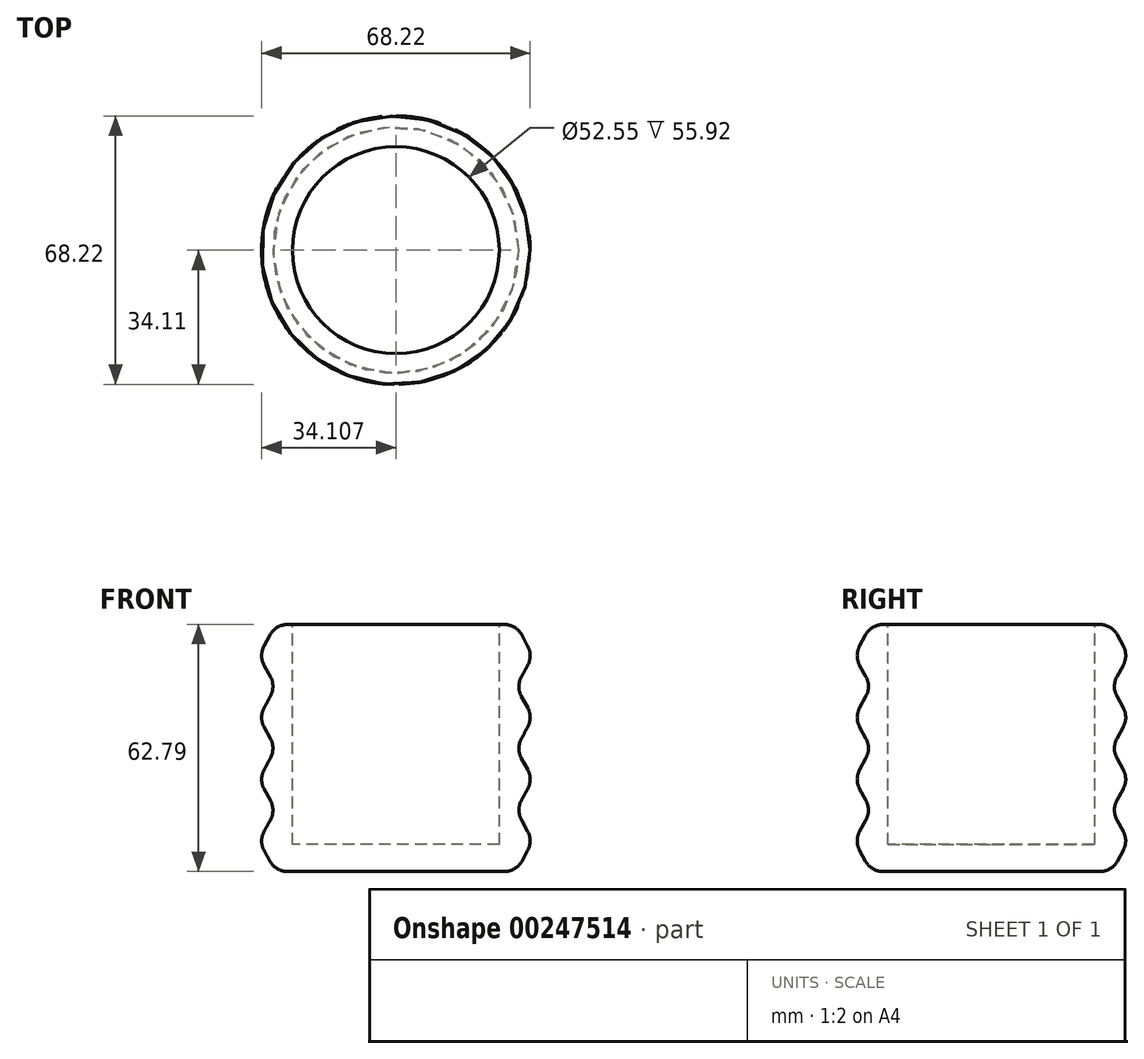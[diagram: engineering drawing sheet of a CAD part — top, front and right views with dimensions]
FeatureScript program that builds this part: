
annotation { "Feature Type Name" : "Feature", "Feature Type Description" : "" }
export const myFeature = defineFeature(function(context is Context, id is Id, definition is map)
    precondition{}
    {
        {
            var Q0;
            Q0=qCreatedBy(makeId("Front.planeOp"),FACE);
            var sketch = newSketch(context, id + "F0", { "sketchPlane" : qUnion([Q0])});
            skLineSegment(sketch, "E0", {"start": v(-1.87, 0) * mm, "end": v(28.67, 0) * mm});
            skLineSegment(sketch, "E1", {"start": v(28.67, 0) * mm, "end": v(32.94, 7.77) * mm});
            skLineSegment(sketch, "E2", {"start": v(32.94, 7.77) * mm, "end": v(28.67, 15.63) * mm});
            skLineSegment(sketch, "E3", {"start": v(28.67, 15.63) * mm, "end": v(32.94, 23.4) * mm});
            skLineSegment(sketch, "E4", {"start": v(32.94, 23.4) * mm, "end": v(28.67, 31.35) * mm});
            skLineSegment(sketch, "E5", {"start": v(28.67, 31.35) * mm, "end": v(32.94, 39.13) * mm});
            skLineSegment(sketch, "E6", {"start": v(32.94, 39.13) * mm, "end": v(28.67, 47.07) * mm});
            skLineSegment(sketch, "E7", {"start": v(28.67, 47.07) * mm, "end": v(32.94, 54.85) * mm});
            skLineSegment(sketch, "E8", {"start": v(32.94, 54.85) * mm, "end": v(28.67, 62.8) * mm});
            skLineSegment(sketch, "E9", {"start": v(28.67, 62.8) * mm, "end": v(24.4, 62.8) * mm});
            skLineSegment(sketch, "E10", {"start": v(24.4, 62.8) * mm, "end": v(24.4, 6.87) * mm});
            skLineSegment(sketch, "E11", {"start": v(24.4, 6.87) * mm, "end": v(-1.87, 6.87) * mm});
            skLineSegment(sketch, "E12", {"start": v(-1.87, 6.87) * mm, "end": v(-1.87, 0) * mm});
            skSolve(sketch);
        }
        {
            var Q0;
            Q0=makeQuery(id+"F0.imprint","IMPRINT",FACE,{"disambiguationData":[TD([[makeQuery(id+"F0.imprint","IMPRINT",EDGE,{"derivedFrom":sQuery(id+"F0.wireOp",EDGE,"E0")}),1.0]])]});
            var Q1;
            Q1=sQuery(id+"F0.wireOp",EDGE,"E12");
            revolve(context, id + "F1", {"entities" : qUnion([Q0]), "axis" : qUnion([Q1]), "revolveType" : RevolveType.FULL});
        }
        {
            var Q0;
            Q0=makeQuery(id+"F1.opRevolve","SWEPT_EDGE",EDGE,{"disambiguationData":[OSD([sQuery(id+"F0.wireOp",EDGE,"E8"),sQuery(id+"F0.wireOp",EDGE,"E9")])]});
            var Q1;
            Q1=makeQuery(id+"F1.opRevolve","SWEPT_FACE",FACE,{"disambiguationData":[OSD([sQuery(id+"F0.wireOp",EDGE,"E8")])]});
            fillet(context, id + "F2", {"entities" : qUnion([Q0, Q1]), "radius" : 5.08 * mm, "tangentPropagation" : true, "allowEdgeOverflow" : false});
        }
        {
            var Q0;
            Q0=makeQuery(id+"F1.opRevolve","SWEPT_FACE",FACE,{"disambiguationData":[OSD([sQuery(id+"F0.wireOp",EDGE,"E6")])]});
            var Q1;
            Q1=makeQuery(id+"F1.opRevolve","SWEPT_FACE",FACE,{"disambiguationData":[OSD([sQuery(id+"F0.wireOp",EDGE,"E5")])]});
            fillet(context, id + "F3", {"entities" : qUnion([Q0, Q1]), "radius" : 5.08 * mm, "tangentPropagation" : true, "allowEdgeOverflow" : false});
        }
        {
            var Q0;
            Q0=makeQuery(id+"F1.opRevolve","SWEPT_FACE",FACE,{"disambiguationData":[OSD([sQuery(id+"F0.wireOp",EDGE,"E4")])]});
            var Q1;
            Q1=makeQuery(id+"F1.opRevolve","SWEPT_FACE",FACE,{"disambiguationData":[OSD([sQuery(id+"F0.wireOp",EDGE,"E3")])]});
            fillet(context, id + "F4", {"entities" : qUnion([Q0, Q1]), "radius" : 5.08 * mm, "tangentPropagation" : true, "allowEdgeOverflow" : false});
        }
        {
            var Q0;
            Q0=makeQuery(id+"F1.opRevolve","SWEPT_FACE",FACE,{"disambiguationData":[OSD([sQuery(id+"F0.wireOp",EDGE,"E2")])]});
            var Q1;
            Q1=makeQuery(id+"F1.opRevolve","SWEPT_FACE",FACE,{"disambiguationData":[OSD([sQuery(id+"F0.wireOp",EDGE,"E1")])]});
            fillet(context, id + "F5", {"entities" : qUnion([Q0, Q1]), "radius" : 5.08 * mm, "tangentPropagation" : true, "allowEdgeOverflow" : false});
        }
    });
